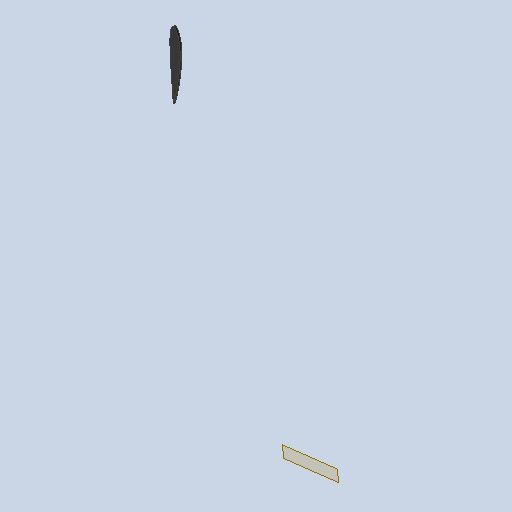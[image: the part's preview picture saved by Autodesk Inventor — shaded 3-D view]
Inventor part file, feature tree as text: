
AUTODESK INVENTOR PART (.ipt)
format: ipt  version: 2025.2 (Build 292293000, 293)  size: 140,288 bytes
history: native  units: in
note: dims shown in document units (in); Inventor stores cm internally (conversion verified against a paired STEP export)
features: reference x6, other x4, extrude x3, sketch x3, projected_geometry x2, plane x1
ambient origin geometry x8: Origin, YZ Plane, XZ Plane, XY Plane, X Axis, Y Axis, Z Axis, Center Point
bodies: Solid1 (feature_tree)
feature tree (19):
  plane  "Work Plane1"
  extrude  "Extrusion1"  Depth=0.5in TaperAngle=0.0deg
  extrude  "Extrusion2"  [1 undecoded]
  extrude  "Extrusion3"  [1 undecoded]
  sketch  "Sketch1"  dims[d0=0.25in d1=0.0in d2=0.5in d3=0.0in]
  reference  "Reference1"
  reference  "Reference2"
  sketch  "Sketch2"  dims[d4=0.0in d5=0.0in]
  reference  "Reference3"
  reference  "Reference4"
  reference  "Reference5"
  reference  "Reference6"
  projected_geometry  "Projected Loop1"
  sketch  "Sketch3"
  projected_geometry  "Projected Loop2"
  other  "<userpath>\Downloads\UAV_v0.2.0\UAV_v0.2.0\UAV_Assembly.iam"
  other  "UAV_Assembly.iam"
  other  "MiddleWingL:1"
  other  "LeftAlerion:1"
note: 2 required parameter values undecoded (feature->parameter linkage not recoverable at this tier; creation-order binding heuristic only, values carry confidence <= 0.55)
